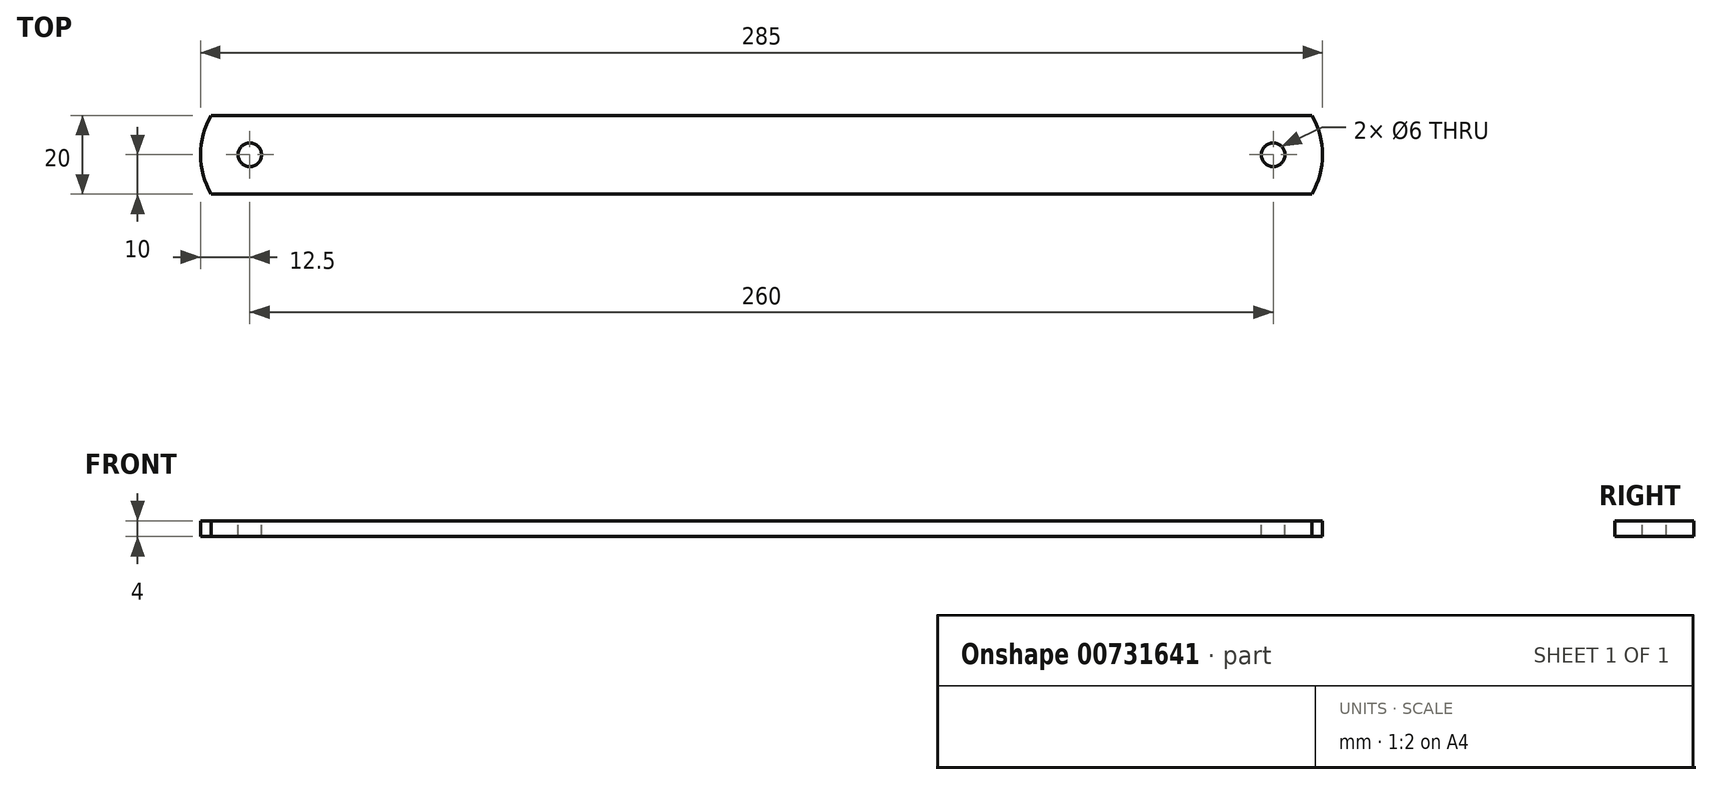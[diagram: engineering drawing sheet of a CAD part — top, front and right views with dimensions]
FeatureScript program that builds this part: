
annotation { "Feature Type Name" : "Feature", "Feature Type Description" : "" }
export const myFeature = defineFeature(function(context is Context, id is Id, definition is map)
    precondition{}
    {
        {
            var Q0;
            Q0=qCreatedBy(makeId("Top.planeOp"),FACE);
            var sketch = newSketch(context, id + "F0", { "sketchPlane" : qUnion([Q0])});
            skLineSegment(sketch, "E0.bottom", {"start": v(0, 0) * mm, "end": v(279.64, 0) * mm});
            skLineSegment(sketch, "E0.top", {"start": v(0, -20) * mm, "end": v(279.64, -20) * mm});
            skArc(sketch, "E1", {"start": v(279.64, -20) * mm, "mid": v(282.32, -10) * mm, "end": v(279.64, 0) * mm});
            skArc(sketch, "E2", {"start": v(0, 0) * mm, "mid": v(-2.68, -10) * mm, "end": v(0, -20) * mm});
            skSolve(sketch);
        }
        {
            var Q0;
            Q0 = qSketchRegion(id + "F0", true);
            extrude(context, id + "F1", {"entities" : qUnion([Q0]), "depth" : 4 * mm, "offsetDistance" : 25 * mm});
        }
        {
            var Q0;
            Q0=makeQuery(id+"F1.opExtrude","CAP_FACE",FACE,{"disambiguationData":[OSD([sQuery(id+"F0.wireOp",EDGE,"E0.bottom"),sQuery(id+"F0.wireOp",EDGE,"E0.top"),sQuery(id+"F0.wireOp",EDGE,"E1"),sQuery(id+"F0.wireOp",EDGE,"E2")])],"isStart":false});
            var sketch = newSketch(context, id + "F2", { "sketchPlane" : qUnion([Q0])});
            skCircle(sketch, "E3", {"center": v(269.82, -10) * mm, "radius": 3 * mm});
            skCircle(sketch, "E4", {"center": v(9.82, -10) * mm, "radius": 3 * mm});
            skSolve(sketch);
        }
        {
            var Q0;
            Q0 = qSketchRegion(id + "F2", true);
            extrude(context, id + "F3", {"entities" : qUnion([Q0]), "operationType" : NewBodyOperationType.REMOVE, "oppositeDirection" : true, "depth" : 4 * mm, "offsetDistance" : 25 * mm});
        }
    });
